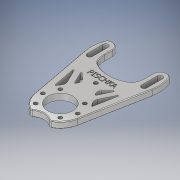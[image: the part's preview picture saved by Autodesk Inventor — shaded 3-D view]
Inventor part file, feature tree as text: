
AUTODESK INVENTOR PART (.ipt)
format: ipt  version: 2019.4 (Build 234330000, 330)  size: 692,736 bytes
history: native  units: mm
features: thread x7, sketch x3, emboss x2, fillet x2, extrude x1, chamfer x1, other x1
ambient origin geometry x8: Origin, YZ Plane, XZ Plane, XY Plane, X Axis, Y Axis, Z Axis, Center Point
bodies: Body1 (feature_tree)
feature tree (17):
  extrude  "Extrusion3"  Depth=20.0mm
  thread  "Thread1"  [1 undecoded]
  thread  "Thread2"  [1 undecoded]
  thread  "Thread3"  [1 undecoded]
  thread  "Thread4"  [1 undecoded]
  thread  "Thread5"  [1 undecoded]
  thread  "Thread6"  [1 undecoded]
  thread  "Thread7"  [1 undecoded]
  emboss  "Emboss1"
  emboss  "Emboss2"
  fillet  "Fillet3"  Radius=3.0mm
  fillet  "Fillet5"  [1 undecoded]
  chamfer  "Chamfer3"  Distance=5.0mm
  other  "Center Lines"
  sketch  "Sketch1"  dims[d0=51.0mm d1=20.0mm d3=3.5mm d4=3.5mm d5=7.0mm d9=3.5mm d11=32.0mm d15=4.1mm d24=3.0mm d25=3.0mm d27=45.0deg]
  sketch  "Sketch3"  dims[d29=3.0mm]
  sketch  "Sketch4"  dims[d30=3.0mm d40=5.0mm d41=0.0mm d44=10.0mm d45=0.0mm d46=10.0mm d47=0.0mm d48=10.0mm d49=0.0mm d50=15.0mm d51=52.0mm d53=27.0mm d54=10.0mm d55=0.0mm d56=10.0mm d57=0.0mm d58=10.0mm d59=0.0mm d60=10.0mm d61=0.0mm d65=0.2mm d66=0.0mm d67=3.0mm d68=3.0mm d69=5.0mm d70=25.0mm d71=5.0mm d72=25.0mm d73=0.2mm d74=0.0mm d75=80.25mm d76=7.5mm d77=3.75mm d78=0.0mm d81=6.25mm d82=12.5mm d85=5.0mm d86=4.0mm d91=0.5mm d94=2.0mm d95=0.5mm d96=2.0mm d97=45.0deg d98=15.0deg d99=24.0mm d101=43.0mm d104=2.0mm]
note: 8 required parameter values undecoded (feature->parameter linkage not recoverable at this tier; creation-order binding heuristic only, values carry confidence <= 0.55)
